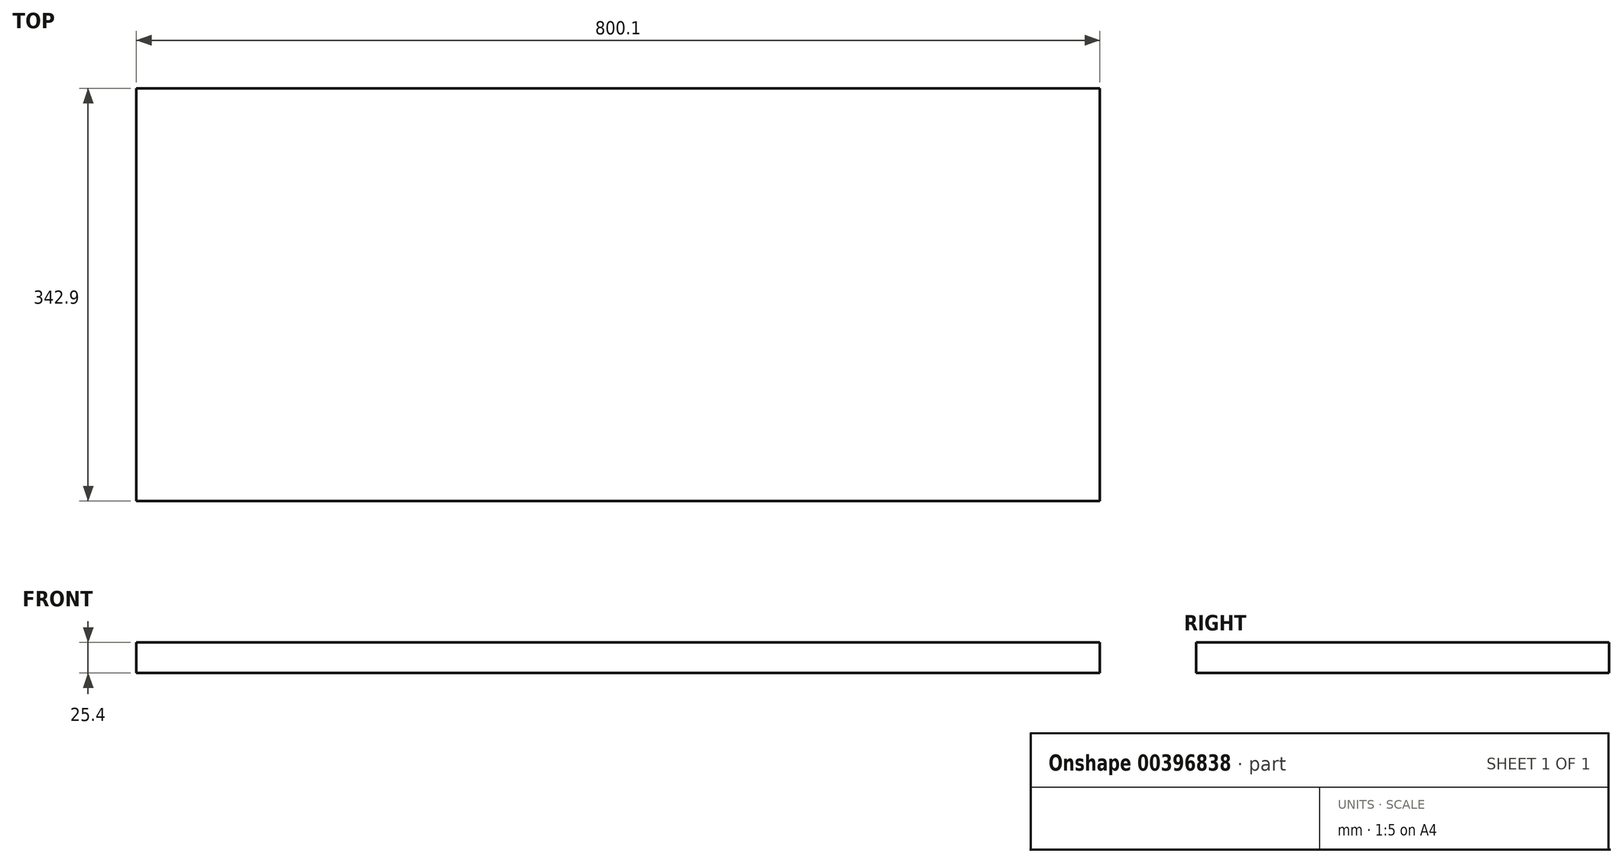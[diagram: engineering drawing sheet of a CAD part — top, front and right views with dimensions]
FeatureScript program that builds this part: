
annotation { "Feature Type Name" : "Feature", "Feature Type Description" : "" }
export const myFeature = defineFeature(function(context is Context, id is Id, definition is map)
    precondition{}
    {
        {
            var Q0;
            Q0=qCreatedBy(makeId("Top.planeOp"),FACE);
            var sketch = newSketch(context, id + "F0", { "sketchPlane" : qUnion([Q0])});
            skLineSegment(sketch, "E0.bottom", {"start": v(-400.05, 171.45) * mm, "end": v(400.05, 171.45) * mm});
            skLineSegment(sketch, "E0.top", {"start": v(-400.05, -171.45) * mm, "end": v(400.05, -171.45) * mm});
            skLineSegment(sketch, "E0.left", {"start": v(-400.05, 171.45) * mm, "end": v(-400.05, -171.45) * mm});
            skLineSegment(sketch, "E0.right", {"start": v(400.05, 171.45) * mm, "end": v(400.05, -171.45) * mm});
            skPoint(sketch, "E0.middle", {"position": v(0, 0) * mm});
            skSolve(sketch);
        }
        {
            var Q0;
            Q0=makeQuery(id+"F0.imprint","IMPRINT",FACE,{"disambiguationData":[TD([[makeQuery(id+"F0.imprint","IMPRINT",EDGE,{"derivedFrom":sQuery(id+"F0.wireOp",EDGE,"E0.bottom")}),-1.0]])]});
            extrude(context, id + "F1", {"entities" : qUnion([Q0]), "depth" : 25.4 * mm});
        }
    });
